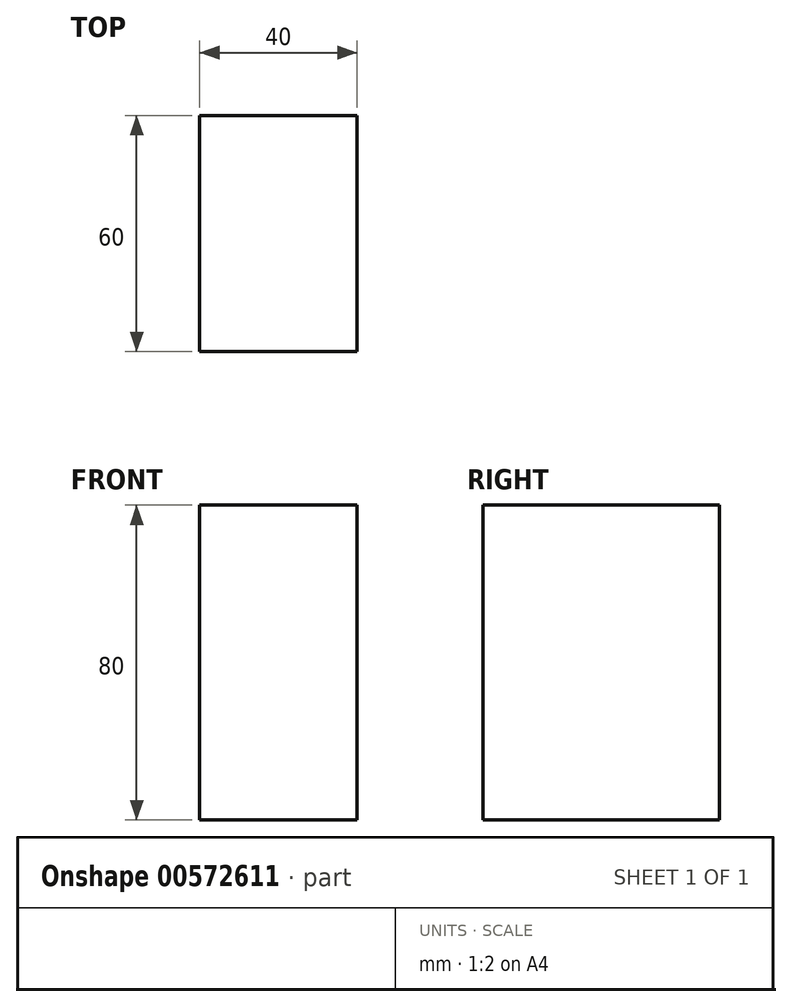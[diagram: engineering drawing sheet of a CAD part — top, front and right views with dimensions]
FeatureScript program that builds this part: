
annotation { "Feature Type Name" : "Feature", "Feature Type Description" : "" }
export const myFeature = defineFeature(function(context is Context, id is Id, definition is map)
    precondition{}
    {
        {
            var Q0;
            Q0=qCreatedBy(makeId("Top.planeOp"),FACE);
            var sketch = newSketch(context, id + "F0", { "sketchPlane" : qUnion([Q0])});
            skLineSegment(sketch, "E0.bottom", {"start": v(0, 0) * mm, "end": v(40, 0) * mm});
            skLineSegment(sketch, "E0.top", {"start": v(0, 60) * mm, "end": v(40, 60) * mm});
            skLineSegment(sketch, "E0.left", {"start": v(0, 0) * mm, "end": v(0, 60) * mm});
            skLineSegment(sketch, "E0.right", {"start": v(40, 0) * mm, "end": v(40, 60) * mm});
            skSolve(sketch);
        }
        {
            var Q0;
            Q0 = qSketchRegion(id + "F0", true);
            var Q1;
            Q1=makeQuery(id+"F0.imprint","IMPRINT",FACE,{"disambiguationData":[TD([[makeQuery(id+"F0.imprint","IMPRINT",EDGE,{"derivedFrom":sQuery(id+"F0.wireOp",EDGE,"E0.bottom")}),1.0]])]});
            extrude(context, id + "F1", {"entities" : qUnion([Q0, Q1]), "depth" : 80 * mm, "offsetDistance" : 25 * mm});
        }
    });
